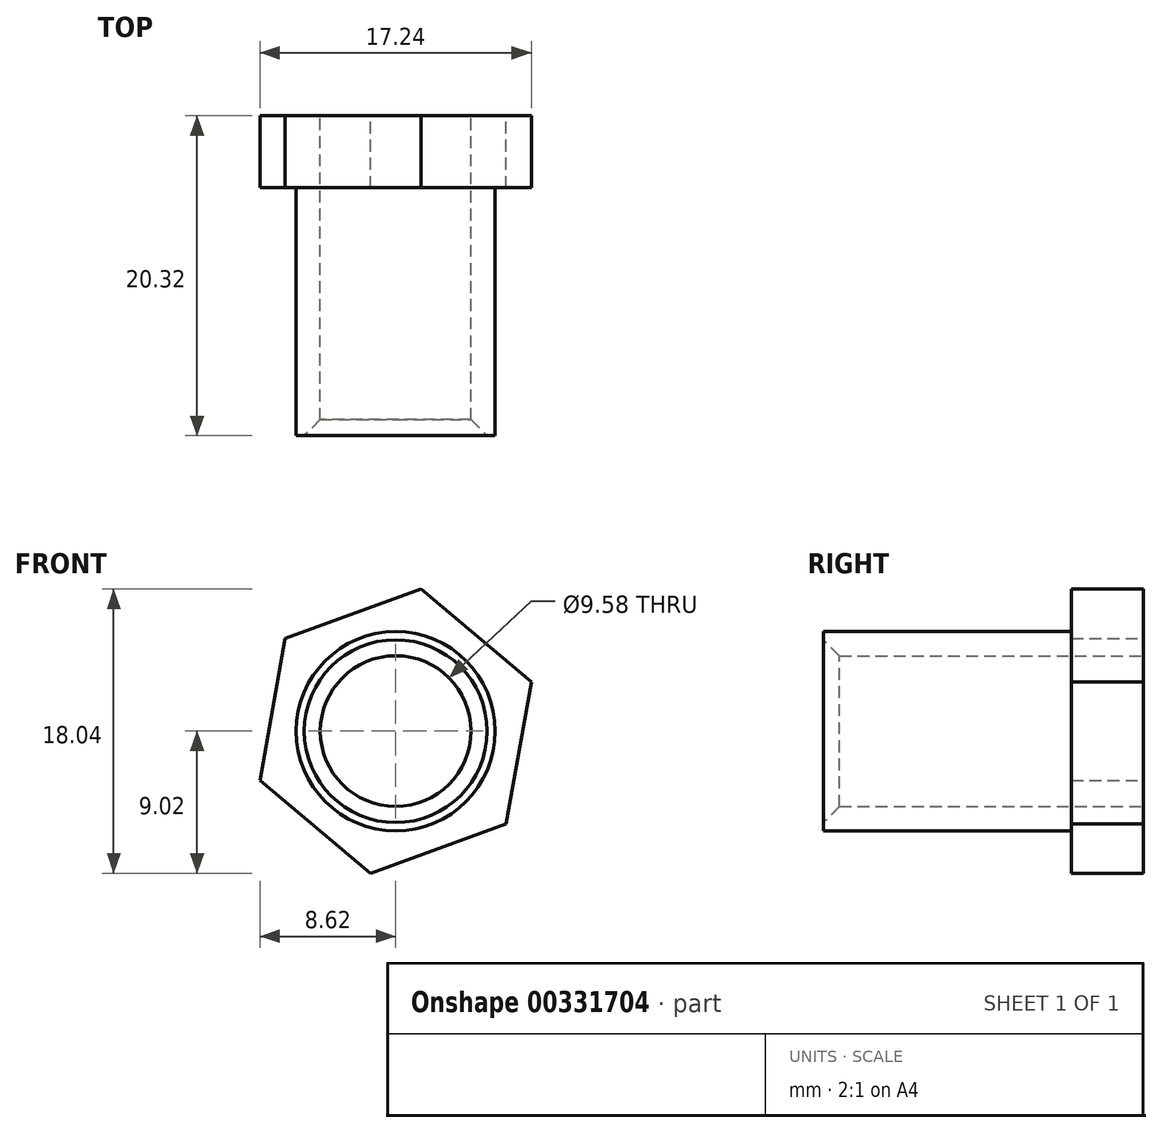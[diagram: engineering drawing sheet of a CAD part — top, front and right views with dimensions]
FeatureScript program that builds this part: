
annotation { "Feature Type Name" : "Feature", "Feature Type Description" : "" }
export const myFeature = defineFeature(function(context is Context, id is Id, definition is map)
    precondition{}
    {
        {
            var Q0;
            Q0=qCreatedBy(makeId("Front.planeOp"),FACE);
            var sketch = newSketch(context, id + "F0", { "sketchPlane" : qUnion([Q0])});
            skCircle(sketch, "E0", {"center": v(0, 0) * mm, "radius": 4.79 * mm});
            skCircle(sketch, "E1", {"center": v(0, 0) * mm, "radius": 6.32 * mm});
            skCircle(sketch, "E2.cCircle", {"center": v(0, 0) * mm, "radius": 7.94 * mm, "construction": true});
            skLineSegment(sketch, "E2.0", {"start": v(8.62, 3.13) * mm, "end": v(7.02, -5.9) * mm});
            skLineSegment(sketch, "E2.1", {"start": v(7.02, -5.9) * mm, "end": v(-1.6, -9.02) * mm});
            skLineSegment(sketch, "E2.2", {"start": v(-1.6, -9.02) * mm, "end": v(-8.62, -3.13) * mm});
            skLineSegment(sketch, "E2.3", {"start": v(-8.62, -3.13) * mm, "end": v(-7.02, 5.9) * mm});
            skLineSegment(sketch, "E2.4", {"start": v(-7.02, 5.9) * mm, "end": v(1.6, 9.02) * mm});
            skLineSegment(sketch, "E2.5", {"start": v(1.6, 9.02) * mm, "end": v(8.62, 3.13) * mm});
            skPoint(sketch, "E2.0.midPoint", {"position": v(7.82, -1.39) * mm});
            skSolve(sketch);
        }
        {
            var Q0;
            Q0=makeQuery(id+"F0.imprint","IMPRINT",FACE,{"disambiguationData":[TD([[makeQuery(id+"F0.imprint","IMPRINT",EDGE,{"derivedFrom":sQuery(id+"F0.wireOp",EDGE,"E0")}),-1.0]])]});
            extrude(context, id + "F1", {"entities" : qUnion([Q0]), "depth" : 20.32 * mm});
        }
        {
            var Q0;
            Q0=makeQuery(id+"F0.imprint","IMPRINT",FACE,{"disambiguationData":[TD([[makeQuery(id+"F0.imprint","IMPRINT",EDGE,{"derivedFrom":sQuery(id+"F0.wireOp",EDGE,"E1")}),-1.0]])]});
            extrude(context, id + "F2", {"entities" : qUnion([Q0]), "operationType" : NewBodyOperationType.ADD, "depth" : 4.57 * mm});
        }
        {
            var Q0;
            Q0=makeQuery(id+"F1.opExtrude","CAP_EDGE",EDGE,{"disambiguationData":[OSD([sQuery(id+"F0.wireOp",EDGE,"E0")])],"isStart":false});
            chamfer(context, id + "F3", {"entities" : qUnion([Q0]), "width" : 1.02 * mm, "tangentPropagation" : true});
        }
    });
